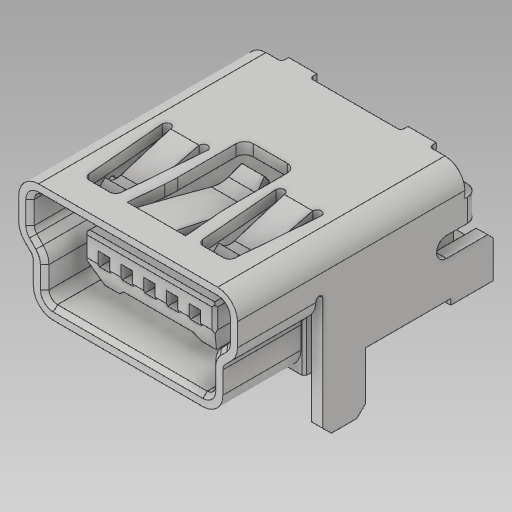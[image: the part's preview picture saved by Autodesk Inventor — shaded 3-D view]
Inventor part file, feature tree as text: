
AUTODESK INVENTOR PART (.ipt)
format: ipt  version: 2020 (Build 240168000, 168)  size: 569,856 bytes
history: native  units: in
note: dims shown in document units (in); Inventor stores cm internally (conversion verified against a paired STEP export)
features: plane x2, imported_body x1
ambient origin geometry x8: Origin, YZ Plane, XZ Plane, XY Plane, X Axis, Y Axis, Z Axis, Center Point
bodies: Solid1 (feature_tree)
feature tree (3):
  plane  "Work Plane1"
  plane  "Work Plane2"
  imported_body  "Imported1"
